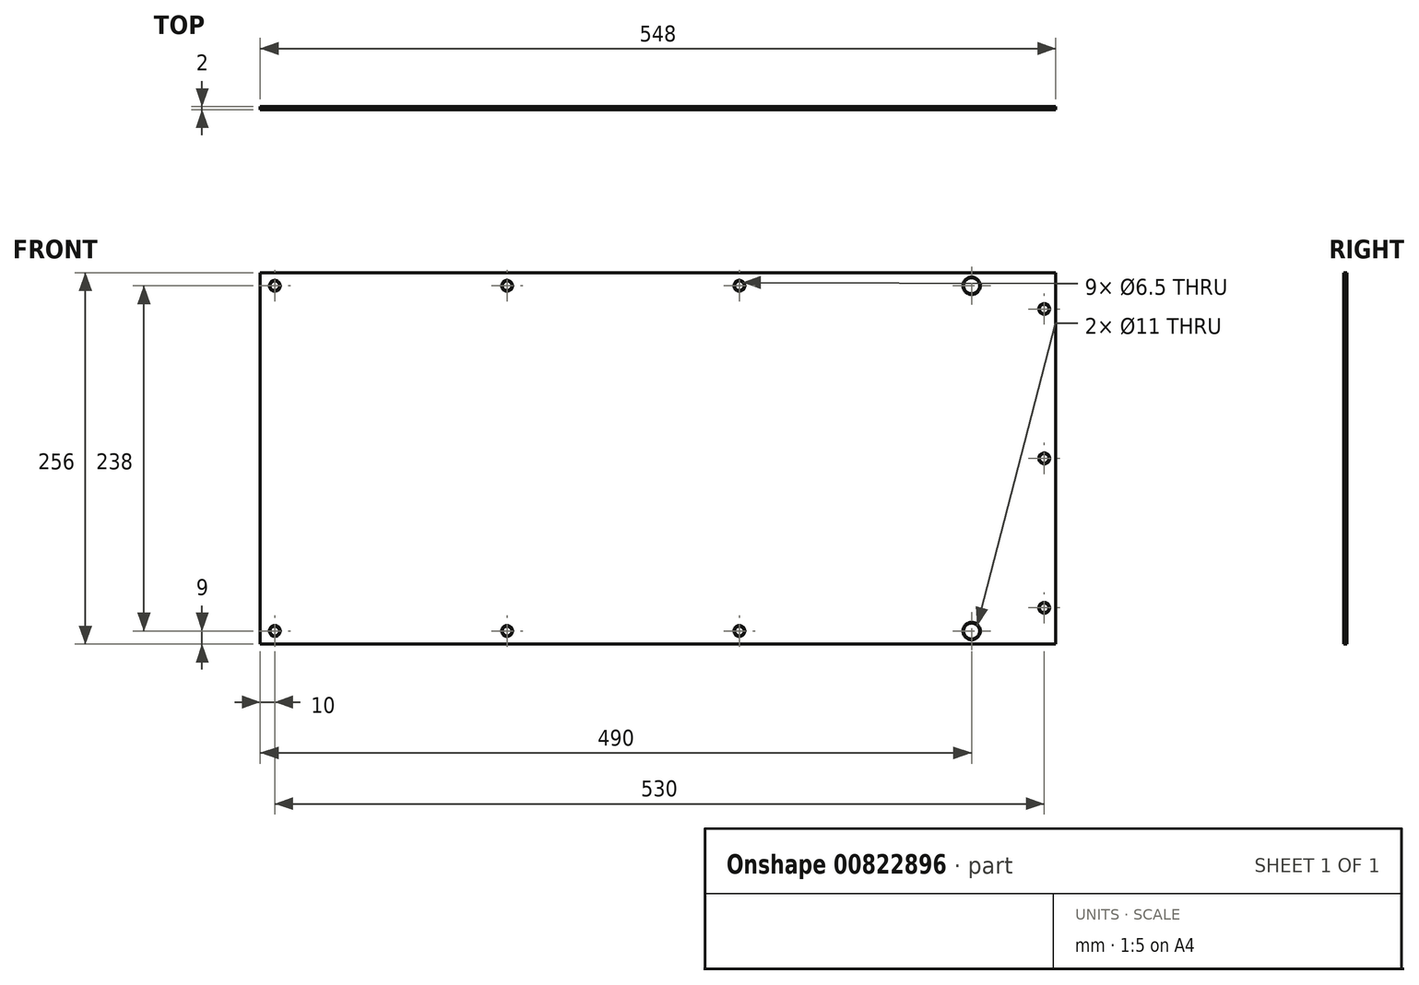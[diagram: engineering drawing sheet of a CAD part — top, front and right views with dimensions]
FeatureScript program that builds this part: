
annotation { "Feature Type Name" : "Feature", "Feature Type Description" : "" }
export const myFeature = defineFeature(function(context is Context, id is Id, definition is map)
    precondition{}
    {
        {
            var Q0;
            Q0=qCreatedBy(makeId("Front.planeOp"),FACE);
            var sketch = newSketch(context, id + "F0", { "sketchPlane" : qUnion([Q0])});
            skLineSegment(sketch, "E0.bottom", {"start": v(-274, -128) * mm, "end": v(274, -128) * mm});
            skLineSegment(sketch, "E0.top", {"start": v(-274, 128) * mm, "end": v(274, 128) * mm});
            skLineSegment(sketch, "E0.left", {"start": v(-274, -128) * mm, "end": v(-274, 128) * mm});
            skLineSegment(sketch, "E0.right", {"start": v(274, -128) * mm, "end": v(274, 128) * mm});
            skPoint(sketch, "E0.middle", {"position": v(0, 0) * mm});
            skLineSegment(sketch, "E1.0", {"start": v(-265, -119) * mm, "end": v(265, -119) * mm, "construction": true});
            skLineSegment(sketch, "E1.1", {"start": v(-265, -119) * mm, "end": v(-265, 119) * mm, "construction": true});
            skLineSegment(sketch, "E1.2", {"start": v(-265, 119) * mm, "end": v(265, 119) * mm, "construction": true});
            skLineSegment(sketch, "E2", {"start": v(0, 0) * mm, "end": v(274, 0) * mm, "construction": true});
            skLineSegment(sketch, "E3", {"start": v(0, 128) * mm, "end": v(0, 0) * mm, "construction": true});
            skCircle(sketch, "E4", {"center": v(216, 119) * mm, "radius": 3.25 * mm, "construction": true});
            skCircle(sketch, "E5", {"center": v(266, 103) * mm, "radius": 3.25 * mm});
            skCircle(sketch, "E6", {"center": v(266, 0) * mm, "radius": 3.25 * mm});
            skCircle(sketch, "E7", {"center": v(-264, 119) * mm, "radius": 3.25 * mm});
            skCircle(sketch, "E8", {"center": v(-104, 119) * mm, "radius": 3.25 * mm});
            skCircle(sketch, "E9", {"center": v(56, 119) * mm, "radius": 3.25 * mm});
            skCircle(sketch, "E10.MirrorC", {"center": v(266, -103) * mm, "radius": 3.25 * mm});
            skCircle(sketch, "E11.MirrorC", {"center": v(-264, -119) * mm, "radius": 3.25 * mm});
            skCircle(sketch, "E12.MirrorC", {"center": v(216, -119) * mm, "radius": 3.25 * mm, "construction": true});
            skCircle(sketch, "E13.MirrorC", {"center": v(-104, -119) * mm, "radius": 3.25 * mm});
            skCircle(sketch, "E14.MirrorC", {"center": v(56, -119) * mm, "radius": 3.25 * mm});
            skCircle(sketch, "E15", {"center": v(216, 119) * mm, "radius": 5.5 * mm});
            skCircle(sketch, "E16.MirrorC", {"center": v(216, -119) * mm, "radius": 5.5 * mm});
            skLineSegment(sketch, "E17", {"start": v(266, 103) * mm, "end": v(266, 0) * mm, "construction": true});
            skLineSegment(sketch, "E18", {"start": v(266, 0) * mm, "end": v(266, -103) * mm, "construction": true});
            skSolve(sketch);
        }
        {
            var Q0;
            Q0 = qSketchRegion(id + "F0", true);
            extrude(context, id + "F1", {"entities" : qUnion([Q0]), "depth" : 2 * mm, "offsetDistance" : 25 * mm});
        }
        {
            var Q0;
            Q0=makeQuery(id+"F1.opExtrude","SWEPT_FACE",FACE,{"disambiguationData":[OSD([sQuery(id+"F0.wireOp",EDGE,"E7")])]});
            var Q1;
            Q1=makeQuery(id+"F1.opExtrude","SWEPT_FACE",FACE,{"disambiguationData":[OSD([sQuery(id+"F0.wireOp",EDGE,"E8")])]});
            var Q2;
            Q2=makeQuery(id+"F1.opExtrude","SWEPT_FACE",FACE,{"disambiguationData":[OSD([sQuery(id+"F0.wireOp",EDGE,"E9")])]});
            var Q3;
            Q3=makeQuery(id+"F1.opExtrude","SWEPT_FACE",FACE,{"disambiguationData":[OSD([sQuery(id+"F0.wireOp",EDGE,"E4")])]});
            var Q4;
            Q4=makeQuery(id+"F1.opExtrude","SWEPT_FACE",FACE,{"disambiguationData":[OSD([sQuery(id+"F0.wireOp",EDGE,"E5")])]});
            var Q5;
            Q5=makeQuery(id+"F1.opExtrude","SWEPT_FACE",FACE,{"disambiguationData":[OSD([sQuery(id+"F0.wireOp",EDGE,"E6")])]});
            var Q6;
            Q6=makeQuery(id+"F1.opExtrude","SWEPT_FACE",FACE,{"disambiguationData":[OSD([sQuery(id+"F0.wireOp",EDGE,"E10.MirrorC")])]});
            var Q7;
            Q7=makeQuery(id+"F1.opExtrude","SWEPT_FACE",FACE,{"disambiguationData":[OSD([sQuery(id+"F0.wireOp",EDGE,"E12.MirrorC")])]});
            var Q8;
            Q8=makeQuery(id+"F1.opExtrude","SWEPT_FACE",FACE,{"disambiguationData":[OSD([sQuery(id+"F0.wireOp",EDGE,"E14.MirrorC")])]});
            var Q9;
            Q9=makeQuery(id+"F1.opExtrude","SWEPT_FACE",FACE,{"disambiguationData":[OSD([sQuery(id+"F0.wireOp",EDGE,"E13.MirrorC")])]});
            var Q10;
            Q10=makeQuery(id+"F1.opExtrude","SWEPT_FACE",FACE,{"disambiguationData":[OSD([sQuery(id+"F0.wireOp",EDGE,"E11.MirrorC")])]});
            var Q11;
            Q11=makeQuery(id+"F1.opExtrude","SWEPT_FACE",FACE,{"disambiguationData":[OSD([sQuery(id+"F0.wireOp",EDGE,"E15")])]});
            var Q12;
            Q12=makeQuery(id+"F1.opExtrude","SWEPT_FACE",FACE,{"disambiguationData":[OSD([sQuery(id+"F0.wireOp",EDGE,"E16.MirrorC")])]});
            chamfer(context, id + "F2", {"entities" : qUnion([Q0, Q1, Q2, Q3, Q4, Q5, Q6, Q7, Q8, Q9, Q10, Q11, Q12]), "width" : 0.5 * mm, "tangentPropagation" : true});
        }
    });
